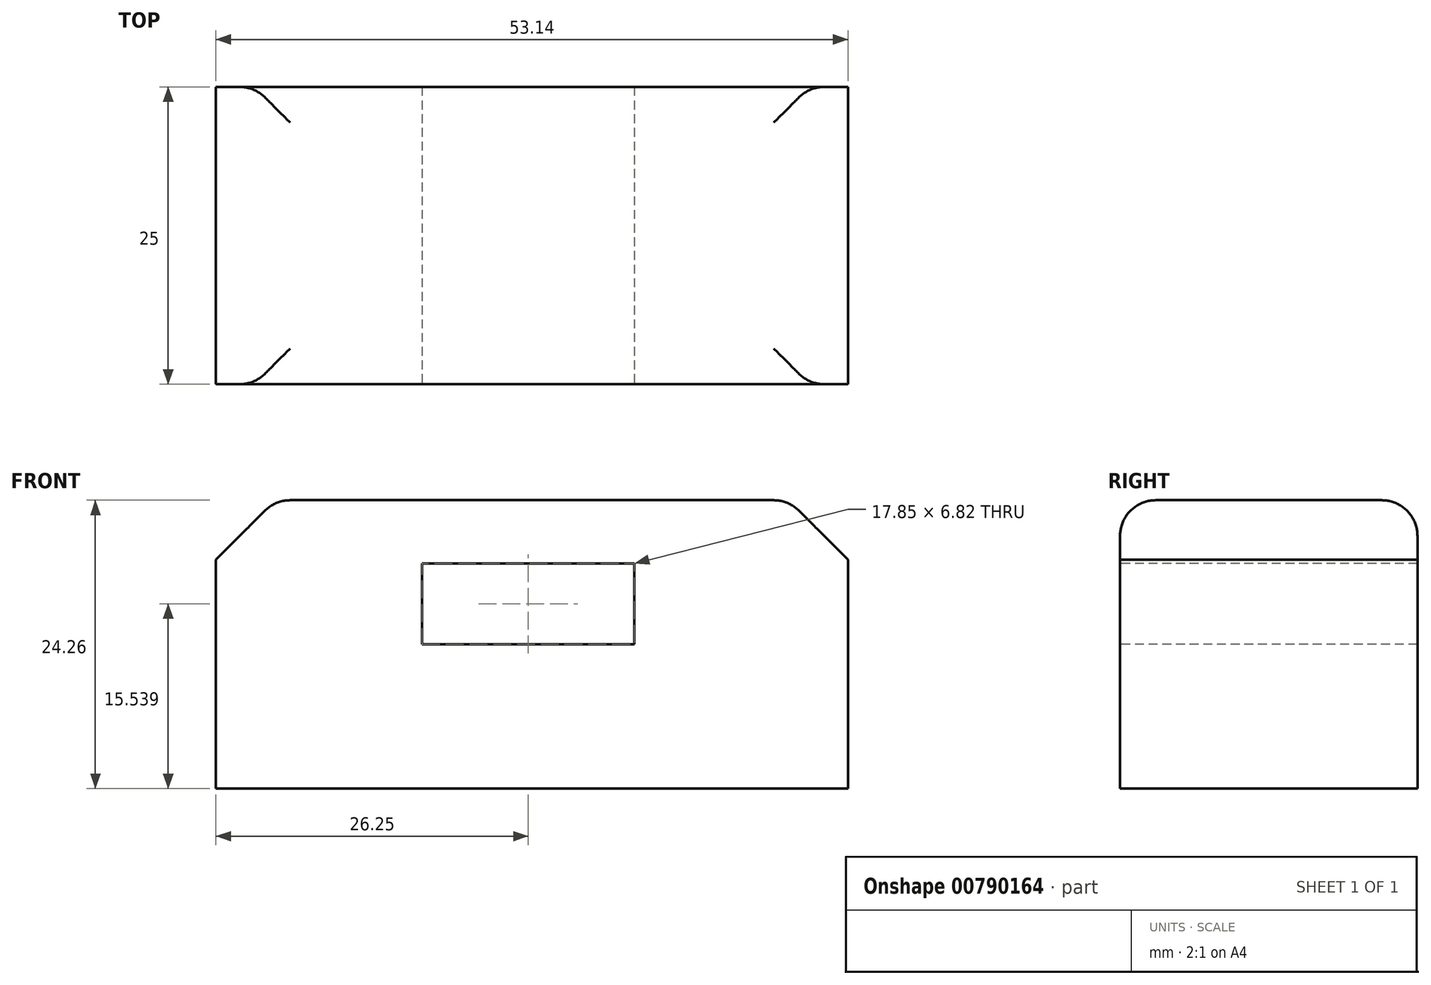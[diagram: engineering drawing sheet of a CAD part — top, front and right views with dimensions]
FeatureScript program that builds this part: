
annotation { "Feature Type Name" : "Feature", "Feature Type Description" : "" }
export const myFeature = defineFeature(function(context is Context, id is Id, definition is map)
    precondition{}
    {
        {
            var Q0;
            Q0=qCreatedBy(makeId("Front.planeOp"),FACE);
            var sketch = newSketch(context, id + "F0", { "sketchPlane" : qUnion([Q0])});
            skLineSegment(sketch, "E0.bottom", {"start": v(26.57, -12.13) * mm, "end": v(-26.57, -12.13) * mm});
            skLineSegment(sketch, "E0.top", {"start": v(26.57, 12.13) * mm, "end": v(-26.57, 12.13) * mm});
            skLineSegment(sketch, "E0.left", {"start": v(-26.57, 12.13) * mm, "end": v(-26.57, -12.13) * mm});
            skLineSegment(sketch, "E0.right", {"start": v(26.57, 12.13) * mm, "end": v(26.57, -12.13) * mm});
            skPoint(sketch, "E0.middle", {"position": v(0, 0) * mm});
            skSolve(sketch);
        }
        {
            var Q0;
            Q0 = qSketchRegion(id + "F0", true);
            extrude(context, id + "F1", {"entities" : qUnion([Q0]), "endBound" : BoundingType.SYMMETRIC, "depth" : 25 * mm, "offsetDistance" : 25 * mm});
        }
        {
            var Q0;
            Q0=makeQuery(id+"F1.opExtrude","CAP_FACE",FACE,{"disambiguationData":[OSD([sQuery(id+"F0.wireOp",EDGE,"E0.bottom"),sQuery(id+"F0.wireOp",EDGE,"E0.top"),sQuery(id+"F0.wireOp",EDGE,"E0.left"),sQuery(id+"F0.wireOp",EDGE,"E0.right")])],"isStart":false});
            var sketch = newSketch(context, id + "F2", { "sketchPlane" : qUnion([Q0])});
            skLineSegment(sketch, "E1.bottom", {"start": v(8.6, 0) * mm, "end": v(-9.24, 0) * mm});
            skLineSegment(sketch, "E1.top", {"start": v(8.6, 6.82) * mm, "end": v(-9.24, 6.82) * mm});
            skLineSegment(sketch, "E1.left", {"start": v(8.6, 0) * mm, "end": v(8.6, 6.82) * mm});
            skLineSegment(sketch, "E1.right", {"start": v(-9.24, 0) * mm, "end": v(-9.24, 6.82) * mm});
            skSolve(sketch);
        }
        {
            var Q0;
            Q0 = qSketchRegion(id + "F2", true);
            extrude(context, id + "F3", {"entities" : qUnion([Q0]), "operationType" : NewBodyOperationType.REMOVE, "oppositeDirection" : true, "depth" : 25 * mm, "offsetDistance" : 25 * mm});
        }
        {
            var Q0;
            Q0=makeQuery(id+"F1.opExtrude","SWEPT_EDGE",EDGE,{"disambiguationData":[OSD([sQuery(id+"F0.wireOp",EDGE,"E0.top"),sQuery(id+"F0.wireOp",EDGE,"E0.left")])]});
            var Q1;
            Q1=makeQuery(id+"F1.opExtrude","SWEPT_EDGE",EDGE,{"disambiguationData":[OSD([sQuery(id+"F0.wireOp",EDGE,"E0.top"),sQuery(id+"F0.wireOp",EDGE,"E0.right")])]});
            chamfer(context, id + "F4", {"entities" : qUnion([Q0, Q1]), "width" : 5 * mm, "tangentPropagation" : true});
        }
        {
            var Q0;
            Q0=makeQuery(id+"F1.opExtrude","CAP_EDGE",EDGE,{"disambiguationData":[OSD([sQuery(id+"F0.wireOp",EDGE,"E0.top")])],"isStart":false});
            var Q1;
            Q1=makeQuery(id+"F1.opExtrude","CAP_EDGE",EDGE,{"disambiguationData":[OSD([sQuery(id+"F0.wireOp",EDGE,"E0.top")])],"isStart":true});
            var Q2;
            {var subQ0=sQuery(id+"F0.wireOp",EDGE,"E0.top");Q2=makeQuery(id+"F4.opChamfer","BLEND_EDGE",EDGE,{"blendedFrom":[makeQuery(id+"F1.opExtrude","SWEPT_EDGE",EDGE,{"disambiguationData":[OSD([subQ0,sQuery(id+"F0.wireOp",EDGE,"E0.left")])]}),makeQuery(id+"F1.opExtrude","SWEPT_FACE",FACE,{"disambiguationData":[OSD([subQ0])]})],"blendedInto":[makeQuery(id+"F1.opExtrude","SWEPT_FACE",FACE,{"disambiguationData":[OSD([subQ0])]})]});}
            var Q3;
            {var subQ0=sQuery(id+"F0.wireOp",EDGE,"E0.top");Q3=makeQuery(id+"F4.opChamfer","BLEND_EDGE",EDGE,{"blendedFrom":[makeQuery(id+"F1.opExtrude","SWEPT_EDGE",EDGE,{"disambiguationData":[OSD([subQ0,sQuery(id+"F0.wireOp",EDGE,"E0.right")])]}),makeQuery(id+"F1.opExtrude","SWEPT_FACE",FACE,{"disambiguationData":[OSD([subQ0])]})],"blendedInto":[makeQuery(id+"F1.opExtrude","SWEPT_FACE",FACE,{"disambiguationData":[OSD([subQ0])]})]});}
            fillet(context, id + "F5", {"entities" : qUnion([Q0, Q1, Q2, Q3]), "radius" : 3 * mm, "tangentPropagation" : true, "allowEdgeOverflow" : false});
        }
    });
